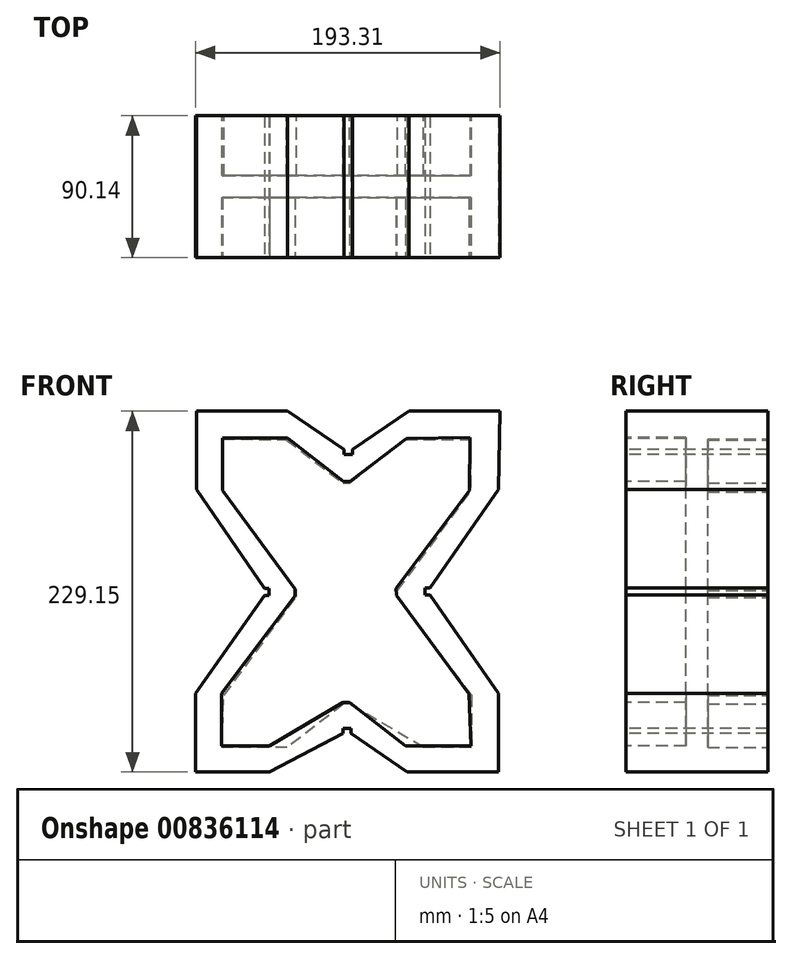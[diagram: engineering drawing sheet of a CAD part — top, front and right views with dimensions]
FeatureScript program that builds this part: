
annotation { "Feature Type Name" : "Feature", "Feature Type Description" : "" }
export const myFeature = defineFeature(function(context is Context, id is Id, definition is map)
    precondition{}
    {
        {
            var Q0;
            Q0=qCreatedBy(makeId("Front.planeOp"),FACE);
            var sketch = newSketch(context, id + "F0", { "sketchPlane" : qUnion([Q0])});
            skLineSegment(sketch, "E0", {"start": v(-69.1, 65.7) * mm, "end": v(-11.2, 65.7) * mm});
            skLineSegment(sketch, "E1", {"start": v(-11.2, 65.7) * mm, "end": v(24.47, 41.2) * mm});
            skLineSegment(sketch, "E2", {"start": v(24.47, 41.2) * mm, "end": v(24.47, 38.18) * mm});
            skLineSegment(sketch, "E3", {"start": v(24.47, 38.18) * mm, "end": v(30, 38.18) * mm});
            skLineSegment(sketch, "E4", {"start": v(30, 38.18) * mm, "end": v(30, 41.2) * mm});
            skLineSegment(sketch, "E5", {"start": v(30, 41.2) * mm, "end": v(65.67, 65.7) * mm});
            skLineSegment(sketch, "E6", {"start": v(65.67, 65.7) * mm, "end": v(123.58, 65.7) * mm});
            skLineSegment(sketch, "E7", {"start": v(123.58, 65.7) * mm, "end": v(122.54, 15.91) * mm});
            skLineSegment(sketch, "E8", {"start": v(122.54, 15.91) * mm, "end": v(79.1, -46.58) * mm});
            skLineSegment(sketch, "E9", {"start": v(79.1, -46.58) * mm, "end": v(76.07, -46.58) * mm});
            skLineSegment(sketch, "E10", {"start": v(76.07, -46.58) * mm, "end": v(76.07, -51.15) * mm});
            skLineSegment(sketch, "E11", {"start": v(76.07, -51.15) * mm, "end": v(79.1, -51.15) * mm});
            skLineSegment(sketch, "E12", {"start": v(79.1, -51.15) * mm, "end": v(122.54, -113.63) * mm});
            skLineSegment(sketch, "E13", {"start": v(122.54, -113.63) * mm, "end": v(122.54, -163.44) * mm});
            skLineSegment(sketch, "E14", {"start": v(122.54, -163.44) * mm, "end": v(64.62, -163.44) * mm});
            skLineSegment(sketch, "E15", {"start": v(-69.1, 65.7) * mm, "end": v(-69.1, 15.9) * mm});
            skLineSegment(sketch, "E16", {"start": v(64.62, -163.44) * mm, "end": v(28.96, -138.93) * mm});
            skLineSegment(sketch, "E17", {"start": v(28.96, -138.93) * mm, "end": v(28.96, -135.91) * mm});
            skLineSegment(sketch, "E18", {"start": v(28.96, -135.91) * mm, "end": v(23.77, -135.91) * mm});
            skLineSegment(sketch, "E19", {"start": v(23.77, -135.91) * mm, "end": v(23.77, -138.94) * mm});
            skLineSegment(sketch, "E20", {"start": v(23.77, -138.94) * mm, "end": v(-22.87, -163.44) * mm});
            skLineSegment(sketch, "E21", {"start": v(-22.87, -163.44) * mm, "end": v(-69.73, -163.44) * mm});
            skLineSegment(sketch, "E22", {"start": v(-69.73, -163.44) * mm, "end": v(-69.73, -113.63) * mm});
            skLineSegment(sketch, "E23", {"start": v(-69.1, 15.9) * mm, "end": v(-26, -46.82) * mm});
            skLineSegment(sketch, "E24", {"start": v(-26, -46.82) * mm, "end": v(-23, -46.82) * mm});
            skLineSegment(sketch, "E25", {"start": v(-23, -46.82) * mm, "end": v(-23, -51.34) * mm});
            skLineSegment(sketch, "E26", {"start": v(-23, -51.34) * mm, "end": v(-26, -51.34) * mm});
            skLineSegment(sketch, "E27", {"start": v(-26, -51.34) * mm, "end": v(-69.73, -113.63) * mm});
            skSolve(sketch);
        }
        {
            var Q0;
            Q0=makeQuery(id+"F0.imprint","IMPRINT",FACE,{"disambiguationData":[TD([[makeQuery(id+"F0.imprint","IMPRINT",EDGE,{"derivedFrom":sQuery(id+"F0.wireOp",EDGE,"E0")}),-1.0]])]});
            extrude(context, id + "F1", {"entities" : qUnion([Q0]), "oppositeDirection" : true, "depth" : 90.14 * mm, "offsetDistance" : 25.4 * mm});
        }
        {
            var Q0;
            Q0=makeQuery(id+"F1.opExtrude","CAP_FACE",FACE,{"disambiguationData":[OSD([sQuery(id+"F0.wireOp",EDGE,"E0"),sQuery(id+"F0.wireOp",EDGE,"E1"),sQuery(id+"F0.wireOp",EDGE,"E2"),sQuery(id+"F0.wireOp",EDGE,"E3"),sQuery(id+"F0.wireOp",EDGE,"E4"),sQuery(id+"F0.wireOp",EDGE,"E5"),sQuery(id+"F0.wireOp",EDGE,"E6"),sQuery(id+"F0.wireOp",EDGE,"E7"),sQuery(id+"F0.wireOp",EDGE,"E8"),sQuery(id+"F0.wireOp",EDGE,"E9"),sQuery(id+"F0.wireOp",EDGE,"E10"),sQuery(id+"F0.wireOp",EDGE,"E11"),sQuery(id+"F0.wireOp",EDGE,"E12"),sQuery(id+"F0.wireOp",EDGE,"E13"),sQuery(id+"F0.wireOp",EDGE,"E14"),sQuery(id+"F0.wireOp",EDGE,"E15"),sQuery(id+"F0.wireOp",EDGE,"E16"),sQuery(id+"F0.wireOp",EDGE,"E17"),sQuery(id+"F0.wireOp",EDGE,"E18"),sQuery(id+"F0.wireOp",EDGE,"E19"),sQuery(id+"F0.wireOp",EDGE,"E20"),sQuery(id+"F0.wireOp",EDGE,"E21"),sQuery(id+"F0.wireOp",EDGE,"E22"),sQuery(id+"F0.wireOp",EDGE,"E23"),sQuery(id+"F0.wireOp",EDGE,"E24"),sQuery(id+"F0.wireOp",EDGE,"E25"),sQuery(id+"F0.wireOp",EDGE,"E26"),sQuery(id+"F0.wireOp",EDGE,"E27")])],"isStart":true});
            cPlane(context, id + "F2", {"entities" : qUnion([Q0]), "cplaneType" : CPlaneType.OFFSET, "offset" : 0 * mm, "width" : 152.4 * mm, "height" : 152.4 * mm});
        }
        {
            var Q0;
            Q0=qCreatedBy(id+"F2.planeOp",FACE);
            var sketch = newSketch(context, id + "F3", { "sketchPlane" : qUnion([Q0])});
            skLineSegment(sketch, "E28", {"start": v(-53.3, -113.75) * mm, "end": v(-6.48, -51.58) * mm});
            skLineSegment(sketch, "E29", {"start": v(-6.48, -51.58) * mm, "end": v(-6.48, -47.3) * mm});
            skLineSegment(sketch, "E30", {"start": v(-6.48, -47.3) * mm, "end": v(-52.6, 15.38) * mm});
            skLineSegment(sketch, "E31", {"start": v(-53.3, -113.75) * mm, "end": v(-53.3, -146.98) * mm});
            skLineSegment(sketch, "E32", {"start": v(23.77, -119.48) * mm, "end": v(28.04, -119.48) * mm});
            skLineSegment(sketch, "E33", {"start": v(-53.3, -146.98) * mm, "end": v(-22.87, -147.02) * mm});
            skLineSegment(sketch, "E34", {"start": v(-22.87, -147.02) * mm, "end": v(23.77, -119.48) * mm});
            skLineSegment(sketch, "E35", {"start": v(28.04, -119.48) * mm, "end": v(63.71, -146.98) * mm});
            skLineSegment(sketch, "E36", {"start": v(63.71, -146.98) * mm, "end": v(105.1, -146.97) * mm});
            skLineSegment(sketch, "E37", {"start": v(105.1, -146.97) * mm, "end": v(103.97, -113.96) * mm});
            skLineSegment(sketch, "E38", {"start": v(103.97, -113.96) * mm, "end": v(57.82, -51.28) * mm});
            skLineSegment(sketch, "E39", {"start": v(57.82, -51.28) * mm, "end": v(57.65, -47.03) * mm});
            skLineSegment(sketch, "E40", {"start": v(57.65, -47.03) * mm, "end": v(104.34, 15.23) * mm});
            skLineSegment(sketch, "E41", {"start": v(104.34, 15.23) * mm, "end": v(104.6, 48.91) * mm});
            skLineSegment(sketch, "E42", {"start": v(104.6, 48.91) * mm, "end": v(64.17, 48.44) * mm});
            skLineSegment(sketch, "E43", {"start": v(64.17, 48.44) * mm, "end": v(28.4, 21.06) * mm});
            skLineSegment(sketch, "E44", {"start": v(28.4, 21.06) * mm, "end": v(24.13, 21.08) * mm});
            skLineSegment(sketch, "E45", {"start": v(24.13, 21.08) * mm, "end": v(-11.43, 48.76) * mm});
            skLineSegment(sketch, "E46", {"start": v(-11.43, 48.76) * mm, "end": v(-52.6, 48.76) * mm});
            skLineSegment(sketch, "E47", {"start": v(-52.6, 48.76) * mm, "end": v(-52.6, 15.38) * mm});
            skSolve(sketch);
        }
        {
            var Q0;
            Q0=makeQuery(id+"F3.imprint","IMPRINT",FACE,{"disambiguationData":[TD([[makeQuery(id+"F3.imprint","IMPRINT",EDGE,{"derivedFrom":sQuery(id+"F3.wireOp",EDGE,"E28")}),-1.0]])]});
            extrude(context, id + "F4", {"entities" : qUnion([Q0]), "operationType" : NewBodyOperationType.REMOVE, "oppositeDirection" : true, "depth" : 38.1 * mm, "offsetDistance" : 25.4 * mm});
        }
        {
            var Q0;
            Q0=makeQuery(id+"F1.opExtrude","CAP_FACE",FACE,{"disambiguationData":[OSD([sQuery(id+"F0.wireOp",EDGE,"E0"),sQuery(id+"F0.wireOp",EDGE,"E1"),sQuery(id+"F0.wireOp",EDGE,"E2"),sQuery(id+"F0.wireOp",EDGE,"E3"),sQuery(id+"F0.wireOp",EDGE,"E4"),sQuery(id+"F0.wireOp",EDGE,"E5"),sQuery(id+"F0.wireOp",EDGE,"E6"),sQuery(id+"F0.wireOp",EDGE,"E7"),sQuery(id+"F0.wireOp",EDGE,"E8"),sQuery(id+"F0.wireOp",EDGE,"E9"),sQuery(id+"F0.wireOp",EDGE,"E10"),sQuery(id+"F0.wireOp",EDGE,"E11"),sQuery(id+"F0.wireOp",EDGE,"E12"),sQuery(id+"F0.wireOp",EDGE,"E13"),sQuery(id+"F0.wireOp",EDGE,"E14"),sQuery(id+"F0.wireOp",EDGE,"E15"),sQuery(id+"F0.wireOp",EDGE,"E16"),sQuery(id+"F0.wireOp",EDGE,"E17"),sQuery(id+"F0.wireOp",EDGE,"E18"),sQuery(id+"F0.wireOp",EDGE,"E19"),sQuery(id+"F0.wireOp",EDGE,"E20"),sQuery(id+"F0.wireOp",EDGE,"E21"),sQuery(id+"F0.wireOp",EDGE,"E22"),sQuery(id+"F0.wireOp",EDGE,"E23"),sQuery(id+"F0.wireOp",EDGE,"E24"),sQuery(id+"F0.wireOp",EDGE,"E25"),sQuery(id+"F0.wireOp",EDGE,"E26"),sQuery(id+"F0.wireOp",EDGE,"E27")])],"isStart":false});
            cPlane(context, id + "F5", {"entities" : qUnion([Q0]), "cplaneType" : CPlaneType.OFFSET, "offset" : 0 * mm, "width" : 152.4 * mm, "height" : 152.4 * mm});
        }
        {
            var Q0;
            Q0=qCreatedBy(id+"F5.planeOp",FACE);
            var sketch = newSketch(context, id + "F6", { "sketchPlane" : qUnion([Q0])});
            skLineSegment(sketch, "E48", {"start": v(-105.46, -114.7) * mm, "end": v(-58.64, -52.54) * mm});
            skLineSegment(sketch, "E49", {"start": v(-58.64, -52.54) * mm, "end": v(-58.64, -48.27) * mm});
            skLineSegment(sketch, "E50", {"start": v(-58.64, -48.27) * mm, "end": v(-104.76, 14.42) * mm});
            skLineSegment(sketch, "E51", {"start": v(-105.46, -114.7) * mm, "end": v(-105.46, -147.94) * mm});
            skLineSegment(sketch, "E52", {"start": v(-28.39, -120.44) * mm, "end": v(-24.12, -120.44) * mm});
            skLineSegment(sketch, "E53", {"start": v(-105.46, -147.94) * mm, "end": v(-75.04, -147.98) * mm});
            skLineSegment(sketch, "E54", {"start": v(-75.04, -147.98) * mm, "end": v(-28.39, -120.44) * mm});
            skLineSegment(sketch, "E55", {"start": v(-24.12, -120.44) * mm, "end": v(11.55, -147.94) * mm});
            skLineSegment(sketch, "E56", {"start": v(11.55, -147.94) * mm, "end": v(52.94, -147.93) * mm});
            skLineSegment(sketch, "E57", {"start": v(52.94, -147.93) * mm, "end": v(51.8, -114.92) * mm});
            skLineSegment(sketch, "E58", {"start": v(51.8, -114.92) * mm, "end": v(5.66, -52.24) * mm});
            skLineSegment(sketch, "E59", {"start": v(5.66, -52.24) * mm, "end": v(5.49, -47.99) * mm});
            skLineSegment(sketch, "E60", {"start": v(5.49, -47.99) * mm, "end": v(52.18, 14.27) * mm});
            skLineSegment(sketch, "E61", {"start": v(52.18, 14.27) * mm, "end": v(52.44, 47.95) * mm});
            skLineSegment(sketch, "E62", {"start": v(52.44, 47.95) * mm, "end": v(12.01, 47.48) * mm});
            skLineSegment(sketch, "E63", {"start": v(12.01, 47.48) * mm, "end": v(-23.77, 20.1) * mm});
            skLineSegment(sketch, "E64", {"start": v(-23.77, 20.1) * mm, "end": v(-28.03, 20.12) * mm});
            skLineSegment(sketch, "E65", {"start": v(-28.03, 20.12) * mm, "end": v(-63.6, 47.8) * mm});
            skLineSegment(sketch, "E66", {"start": v(-63.6, 47.8) * mm, "end": v(-104.76, 47.8) * mm});
            skLineSegment(sketch, "E67", {"start": v(-104.76, 47.8) * mm, "end": v(-104.76, 14.42) * mm});
            skSolve(sketch);
        }
        {
            var Q0;
            Q0=makeQuery(id+"F6.imprint","IMPRINT",FACE,{"disambiguationData":[TD([[makeQuery(id+"F6.imprint","IMPRINT",EDGE,{"derivedFrom":sQuery(id+"F6.wireOp",EDGE,"E48")}),-1.0]])]});
            extrude(context, id + "F7", {"entities" : qUnion([Q0]), "operationType" : NewBodyOperationType.REMOVE, "oppositeDirection" : true, "depth" : 38.1 * mm, "offsetDistance" : 25.4 * mm});
        }
    });
